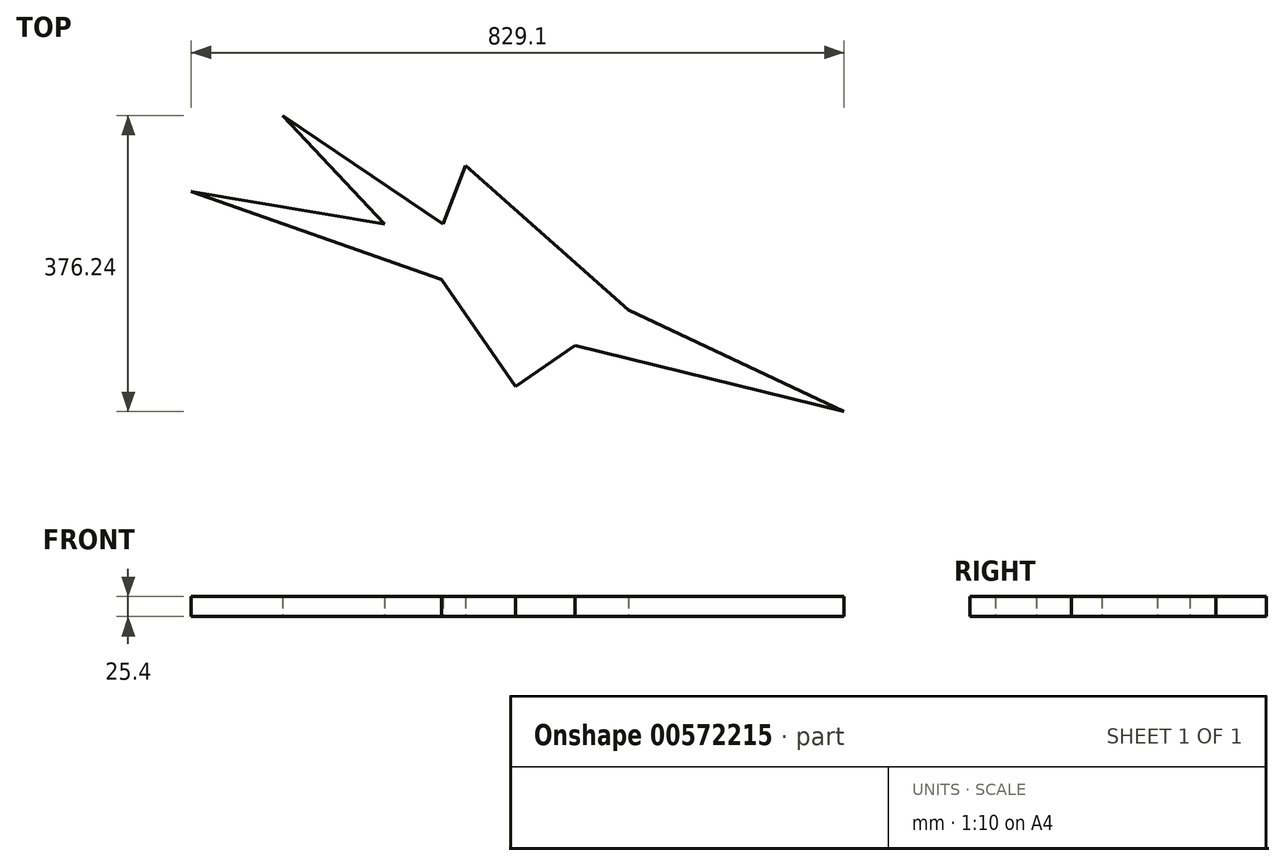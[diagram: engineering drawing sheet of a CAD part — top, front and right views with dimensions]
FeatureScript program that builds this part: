
annotation { "Feature Type Name" : "Feature", "Feature Type Description" : "" }
export const myFeature = defineFeature(function(context is Context, id is Id, definition is map)
    precondition{}
    {
        {
            var Q0;
            Q0=qCreatedBy(makeId("Top.planeOp"),FACE);
            var sketch = newSketch(context, id + "F0", { "sketchPlane" : qUnion([Q0])});
            skLineSegment(sketch, "E0", {"start": v(0, 0) * mm, "end": v(-245.47, 41) * mm});
            skLineSegment(sketch, "E1", {"start": v(-245.47, 41) * mm, "end": v(72.61, -70.52) * mm});
            skLineSegment(sketch, "E2", {"start": v(72.61, -70.52) * mm, "end": v(166.52, -206.16) * mm});
            skLineSegment(sketch, "E3", {"start": v(166.52, -206.16) * mm, "end": v(241.83, -154.01) * mm});
            skLineSegment(sketch, "E4", {"start": v(241.83, -154.01) * mm, "end": v(583.63, -238.2) * mm});
            skLineSegment(sketch, "E5", {"start": v(583.63, -238.2) * mm, "end": v(309.7, -109.43) * mm});
            skLineSegment(sketch, "E6", {"start": v(309.7, -109.43) * mm, "end": v(103.08, 74.3) * mm});
            skLineSegment(sketch, "E7", {"start": v(103.08, 74.3) * mm, "end": v(74.3, 0) * mm});
            skLineSegment(sketch, "E8", {"start": v(74.3, 0) * mm, "end": v(-129.4, 138.04) * mm});
            skLineSegment(sketch, "E9", {"start": v(-129.4, 138.04) * mm, "end": v(0, 0) * mm});
            skSolve(sketch);
        }
        {
            var Q0;
            Q0=makeQuery(id+"F0.imprint","IMPRINT",FACE,{"disambiguationData":[TD([[makeQuery(id+"F0.imprint","IMPRINT",EDGE,{"derivedFrom":sQuery(id+"F0.wireOp",EDGE,"E0")}),1.0]])]});
            extrude(context, id + "F1", {"entities" : qUnion([Q0]), "depth" : 25.4 * mm, "offsetDistance" : 25.4 * mm});
        }
    });
